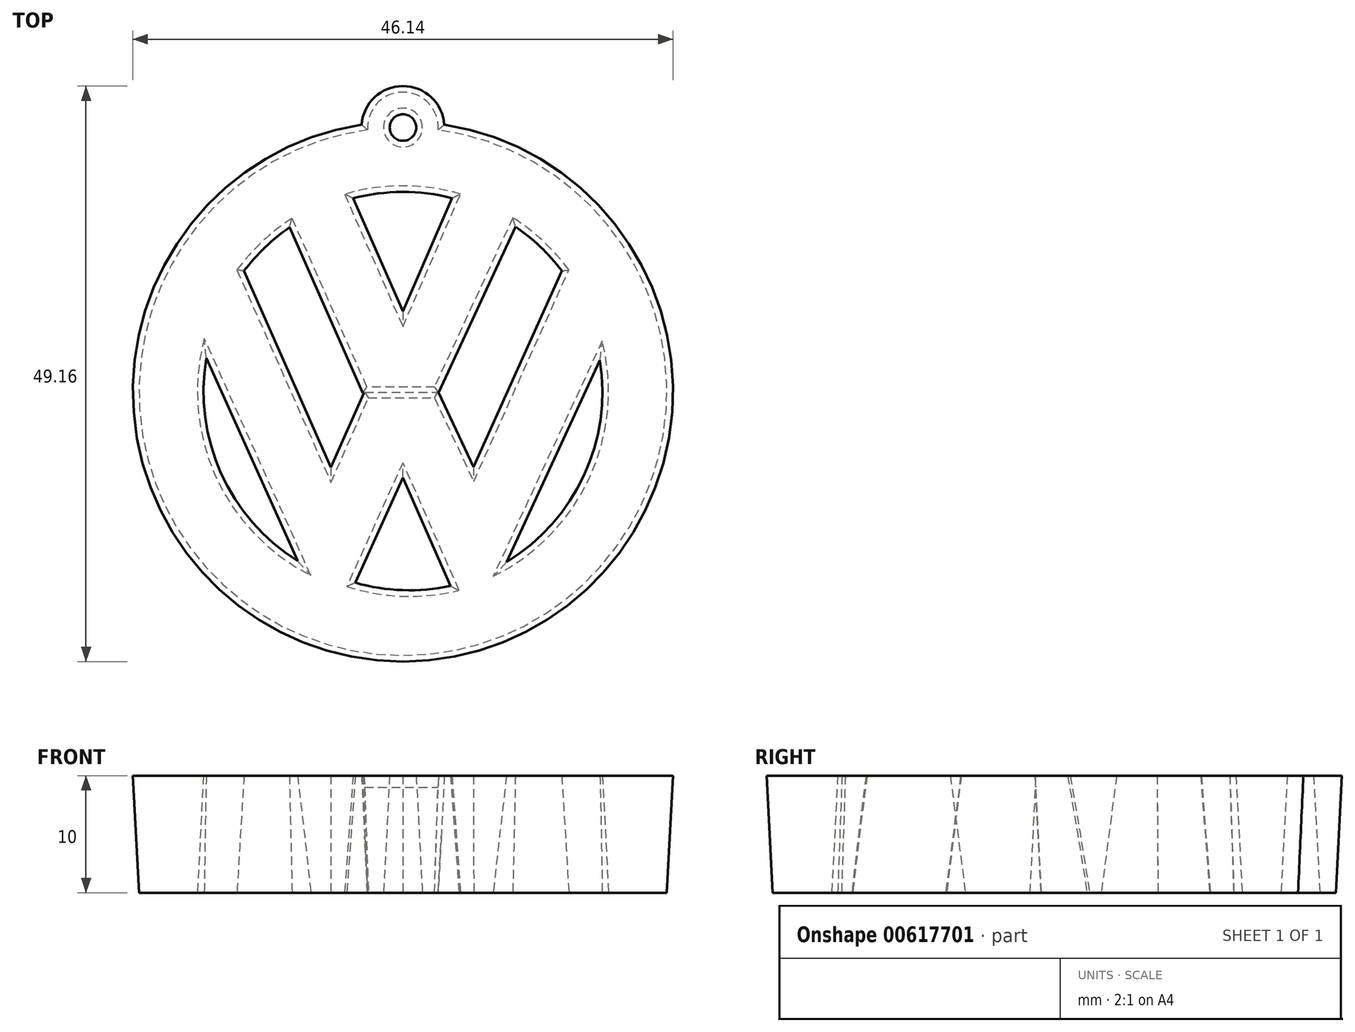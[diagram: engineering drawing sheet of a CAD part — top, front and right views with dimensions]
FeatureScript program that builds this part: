
annotation { "Feature Type Name" : "Feature", "Feature Type Description" : "" }
export const myFeature = defineFeature(function(context is Context, id is Id, definition is map)
    precondition{}
    {
        {
            var Q0;
            Q0=qCreatedBy(makeId("Top.planeOp"),FACE);
            var sketch = newSketch(context, id + "F0", { "sketchPlane" : qUnion([Q0])});
            skLineSegment(sketch, "E0", {"start": v(-5, 16.88) * mm, "end": v(0, 5.53) * mm});
            skLineSegment(sketch, "E1", {"start": v(0, 5.53) * mm, "end": v(4.94, 16.9) * mm});
            skLineSegment(sketch, "E2", {"start": v(-9.49, 14.83) * mm, "end": v(-3.08, 0.4) * mm});
            skLineSegment(sketch, "E3", {"start": v(-14.3, 10.64) * mm, "end": v(-6.15, -7.77) * mm});
            skLineSegment(sketch, "E4", {"start": v(-6.15, -7.77) * mm, "end": v(-2.96, -0.55) * mm});
            skLineSegment(sketch, "E5", {"start": v(-3.08, 0.4) * mm, "end": v(2.7, 0.4) * mm});
            skLineSegment(sketch, "E6", {"start": v(-2.96, -0.55) * mm, "end": v(2.7, -0.55) * mm});
            skLineSegment(sketch, "E7", {"start": v(6.05, -7.69) * mm, "end": v(2.7, -0.55) * mm});
            skLineSegment(sketch, "E8", {"start": v(14.23, 10.49) * mm, "end": v(6.05, -7.69) * mm});
            skLineSegment(sketch, "E9", {"start": v(-17.08, 4.76) * mm, "end": v(-7.74, -16) * mm});
            skLineSegment(sketch, "E10", {"start": v(17.14, 4.56) * mm, "end": v(7.6, -16) * mm});
            skLineSegment(sketch, "E11", {"start": v(0, -6.08) * mm, "end": v(-4.8, -16.66) * mm});
            skLineSegment(sketch, "E12", {"start": v(4.8, -16.99) * mm, "end": v(0, -6.08) * mm});
            skArc(sketch, "E13", {"start": v(7.71, -15.79) * mm, "mid": v(15.94, -7.39) * mm, "end": v(17.03, 4.32) * mm});
            skArc(sketch, "E14.trimOffspring", {"start": v(-16.97, 4.53) * mm, "mid": v(-16.02, -7.2) * mm, "end": v(-7.87, -15.7) * mm});
            skArc(sketch, "E15.trimOffspring", {"start": v(-9.47, 14.8) * mm, "mid": v(-12.03, 12.8) * mm, "end": v(-14.18, 10.37) * mm});
            skArc(sketch, "E16.trimOffspring", {"start": v(14.18, 10.37) * mm, "mid": v(12, 12.84) * mm, "end": v(9.39, 14.85) * mm});
            skLineSegment(sketch, "E17", {"start": v(9.39, 14.85) * mm, "end": v(2.7, 0.4) * mm});
            skArc(sketch, "E18.trimOffspring", {"start": v(4.92, 16.87) * mm, "mid": v(-0.03, 17.57) * mm, "end": v(-4.98, 16.85) * mm});
            skArc(sketch, "E19", {"start": v(-4.8, -16.66) * mm, "mid": v(-0.02, -17.5) * mm, "end": v(4.8, -16.99) * mm});
            skArc(sketch, "E20", {"start": v(-3.01, 22.35) * mm, "mid": v(0, -22.55) * mm, "end": v(3.01, 22.35) * mm});
            skArc(sketch, "E21", {"start": v(3.01, 22.35) * mm, "mid": v(0, 25.57) * mm, "end": v(-3.01, 22.35) * mm});
            skCircle(sketch, "E22", {"center": v(0, 22.55) * mm, "radius": 1.66 * mm});
            skSolve(sketch);
        }
        {
            var Q0;
            Q0 = qSketchRegion(id + "F0", true);
            extrude(context, id + "F1", {"entities" : qUnion([Q0]), "depth" : 10 * mm, "offsetDistance" : 25 * mm, "hasDraft" : true, "draftAngle" : 3 * degree});
        }
    });
